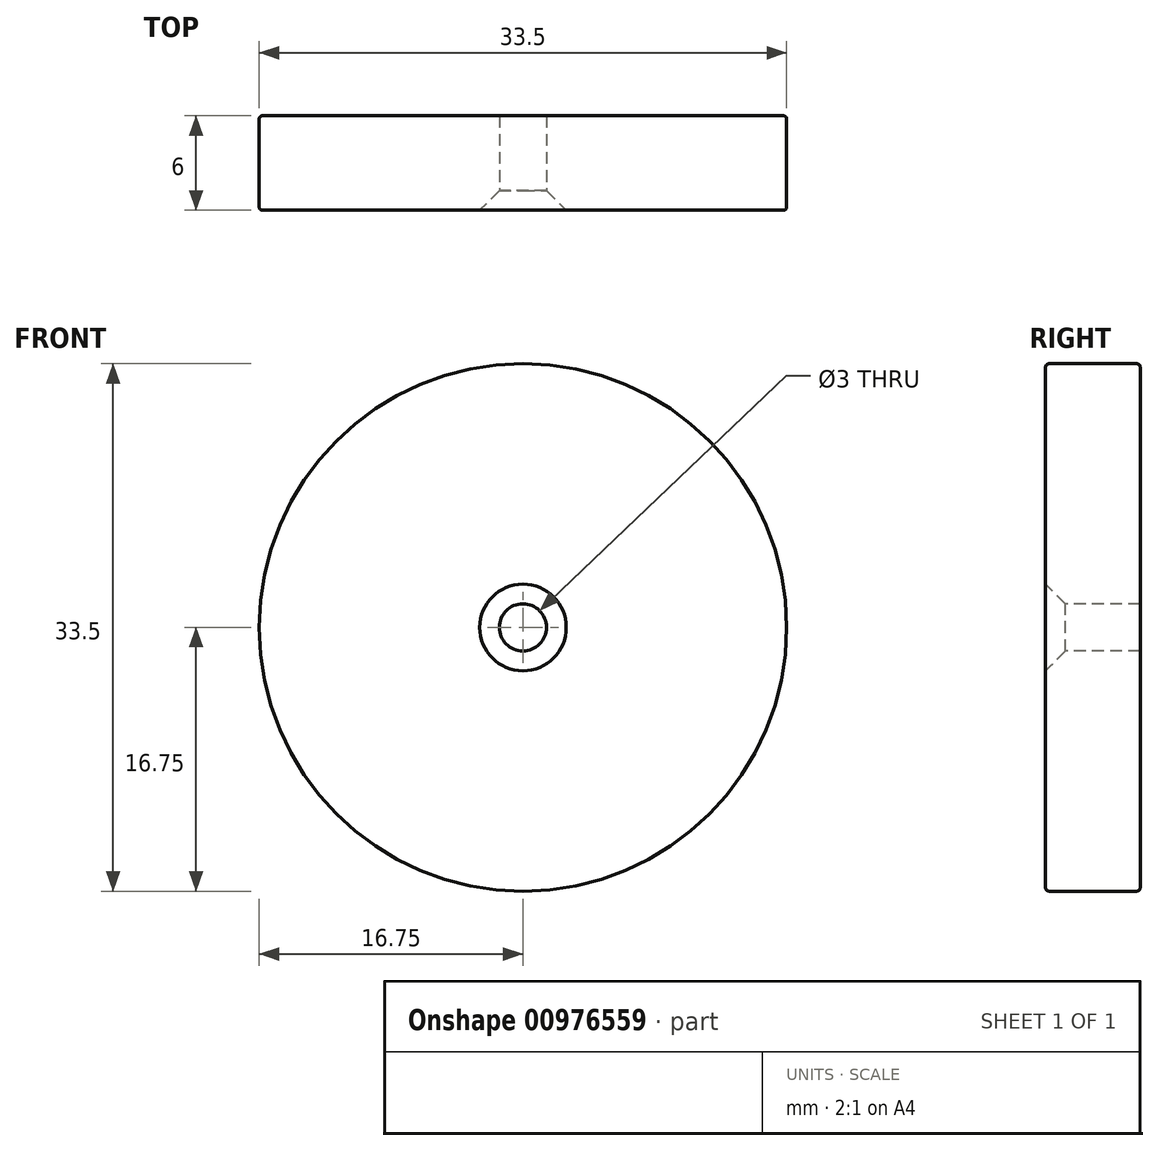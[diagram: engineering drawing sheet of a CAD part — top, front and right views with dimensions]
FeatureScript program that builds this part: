
annotation { "Feature Type Name" : "Feature", "Feature Type Description" : "" }
export const myFeature = defineFeature(function(context is Context, id is Id, definition is map)
    precondition{}
    {
        {
            var Q0;
            Q0=qCreatedBy(makeId("Front.planeOp"),FACE);
            var sketch = newSketch(context, id + "F0", { "sketchPlane" : qUnion([Q0])});
            skCircle(sketch, "E0", {"center": v(0, 0) * mm, "radius": 16.75 * mm});
            skSolve(sketch);
        }
        {
            var Q0;
            Q0=makeQuery(id+"F0.imprint","IMPRINT",FACE,{"disambiguationData":[TD([[makeQuery(id+"F0.imprint","IMPRINT",EDGE,{"derivedFrom":sQuery(id+"F0.wireOp",EDGE,"E0")}),1.0]])]});
            extrude(context, id + "F1", {"entities" : qUnion([Q0]), "depth" : 6 * mm, "offsetDistance" : 25 * mm});
        }
        {
            var Q0;
            Q0=makeQuery(id+"F1.opExtrude","CAP_FACE",FACE,{"disambiguationData":[OSD([sQuery(id+"F0.wireOp",EDGE,"E0")])],"isStart":false});
            var sketch = newSketch(context, id + "F2", { "sketchPlane" : qUnion([Q0])});
            skPoint(sketch, "E1", {"position": v(0, 0) * mm});
            skSolve(sketch);
        }
        {
            var Q0;
            Q0=sQuery(id+"F2.wireOp",VERTEX,"E1");
            var Q1;
            Q1=makeQuery(id+"F1.opExtrude","SWEPT_BODY",BODY,{"disambiguationData":[OSD([sQuery(id+"F0.wireOp",EDGE,"E0")])]});
            hole(context, id + "F3", {"style" : HoleStyle.C_SINK, "endStyle" : HoleEndStyle.THROUGH, "holeDiameter" : 3 * mm, "cSinkDiameter" : 5.5 * mm, "cSinkAngle" : 90 * degree, "majorDiameter" : 5 * mm, "isTappedThrough" : true, "tappedDepth" : 12 * mm, "tapClearance" : 3, "locations" : qUnion([Q0]), "scope" : qUnion([Q1])});
        }
        {
            var Q0;
            Q0=makeQuery(id+"F1.opExtrude","CAP_EDGE",EDGE,{"disambiguationData":[OSD([sQuery(id+"F0.wireOp",EDGE,"E0")])],"isStart":false});
            var Q1;
            Q1=makeQuery(id+"F1.opExtrude","CAP_EDGE",EDGE,{"disambiguationData":[OSD([sQuery(id+"F0.wireOp",EDGE,"E0")])],"isStart":true});
            fillet(context, id + "F4", {"entities" : qUnion([Q0, Q1]), "radius" : .2 * mm, "tangentPropagation" : true, "allowEdgeOverflow" : false});
        }
    });
